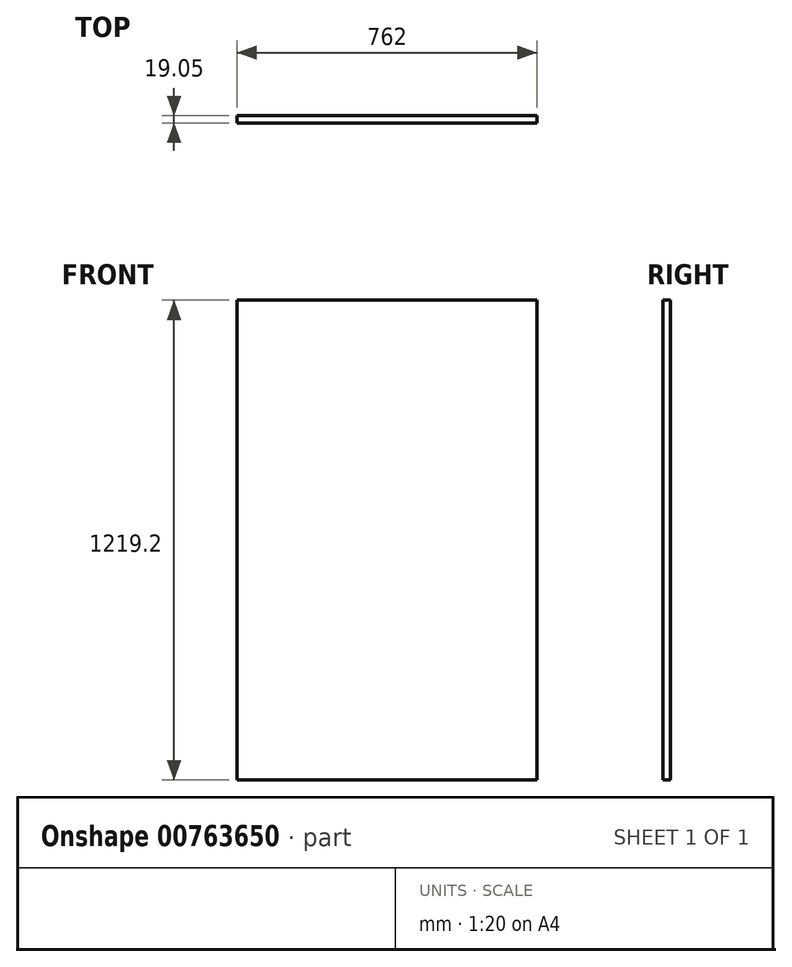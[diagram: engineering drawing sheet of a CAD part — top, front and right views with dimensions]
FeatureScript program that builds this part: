
annotation { "Feature Type Name" : "Feature", "Feature Type Description" : "" }
export const myFeature = defineFeature(function(context is Context, id is Id, definition is map)
    precondition{}
    {
        {
            var Q0;
            Q0=qCreatedBy(makeId("Front.planeOp"),FACE);
            var sketch = newSketch(context, id + "F0", { "sketchPlane" : qUnion([Q0])});
            skLineSegment(sketch, "E0.bottom", {"start": v(381, 609.6) * mm, "end": v(-381, 609.6) * mm});
            skLineSegment(sketch, "E0.top", {"start": v(381, -609.6) * mm, "end": v(-381, -609.6) * mm});
            skLineSegment(sketch, "E0.left", {"start": v(381, 609.6) * mm, "end": v(381, -609.6) * mm});
            skLineSegment(sketch, "E0.right", {"start": v(-381, 609.6) * mm, "end": v(-381, -609.6) * mm});
            skPoint(sketch, "E0.middle", {"position": v(0, 0) * mm});
            skSolve(sketch);
        }
        {
            var Q0;
            Q0 = qSketchRegion(id + "F0", true);
            extrude(context, id + "F1", {"entities" : qUnion([Q0]), "depth" : 19.05 * mm, "offsetDistance" : 25.4 * mm});
        }
    });
